# Revit family: DR1035551_Griferia Lavamanos Monocontrol Alta DRAA
name_source: partatom
category: Plumbing Fixtures
units: mm (PartAtom-declared; Revit-internal decimal feet)

## family parameters
Always vertical = Yes
Cut with Voids When Loaded = No
OmniClass Number = 23.31.11.00
OmniClass Title = Faucets
Part Type = Normal
Room Calculation Point = No
Round Connector Dimension = Use Diameter
Shared = No
Work Plane-Based = No

## types (1)
- DR1035551_Griferia Lavamanos Monocontrol Alta DRAA
    Acabado = Cromado
    Alto = 277 mm  [stored 0.908793 ft]
    Altura de la grifería = Alta
    Ancho = 57 mm  [stored 0.187008 ft]
    Capacidad de flujo = 5.80 l/m máximo a 60 psi
    Colección = Vida
    Consumo de Agua = 5.8 lt
    Creado por = IDD
    Description = La línea Draa cuenta con todos los atributos de diseño y funcionalidad que la hacen perfecta para soluciones en espacios actuales. Ofrece una línea de griferías para ducha, lavamanos y accesorios con la perfecta combinacion de líneas rectas y modernas. Grifería monocontrol ultra ahorro de 5,8 litros por minuto. Estructura robusta que ofrece durabilidad,Grifería que no contamina el agua con plomo. Grifería con chorro circular espumoso.
    Fabricante = Corona
    Fecha de creación = 12/08/2020
    Garantía = 30 años en estructura
    Garantías de otros componentes = 2 años en acabados
    Incluye = Cuerpo, Manija
    Longitud = 185 mm  [stored 0.606955 ft]
    Línea = Draa
    Material = Corona_Laton
    Material Manija = Corona_Zamak
    Presión máxima recomendada = 125 psi (862 Kpa)
    Presión mínima recomendada = 20 psi (138 Kpa)
    Productos compatibles = Lavamanos tipo vessel
    Resistencia = Resistente a la corrosión, pelado y decoloración por agua, Resistente al efecto de jabones y limpiadores de tocador
    Sistema de accionamiento = Palanca
    Tecnologías = EcoStream
    Temperatura de uso = Entre 4˚C y 66˚C
    Tipo de chorro = Espumoso
    Tipo de grifería = Monocontrol
    Tipo de manija / Accionamiento = Palanca
    URL = https://corona.co
    Uso = Residencial

note: [stored X ft] marks values corroborated as IEEE doubles in the binary element streams (Revit-internal decimal feet)

## geometry (parser evidence)
native form markers: Sweep x7
no freeform markers — native parametric forms only
